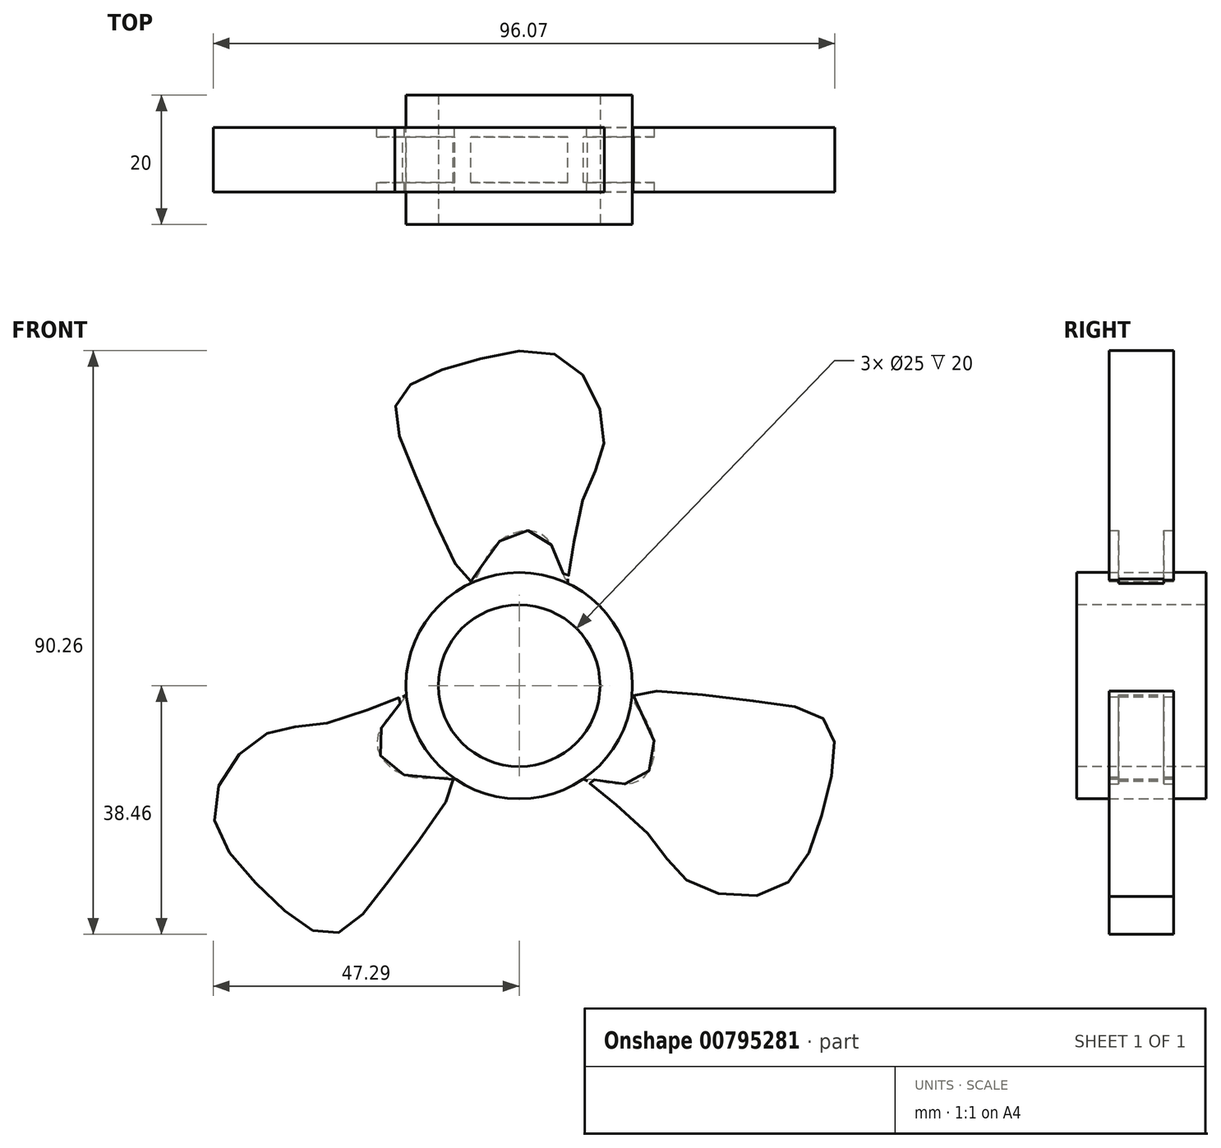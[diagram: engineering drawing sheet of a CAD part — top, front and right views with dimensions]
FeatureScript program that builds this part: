
annotation { "Feature Type Name" : "Feature", "Feature Type Description" : "" }
export const myFeature = defineFeature(function(context is Context, id is Id, definition is map)
    precondition{}
    {
        {
            var Q0;
            Q0=qCreatedBy(makeId("Front.planeOp"),FACE);
            var sketch = newSketch(context, id + "F0", { "sketchPlane" : qUnion([Q0])});
            skCircle(sketch, "E0", {"center": v(0, 0) * mm, "radius": 17.5 * mm});
            skSolve(sketch);
        }
        {
            var Q0;
            Q0=makeQuery(id+"F0.imprint","IMPRINT",FACE,{"disambiguationData":[TD([[makeQuery(id+"F0.imprint","IMPRINT",EDGE,{"derivedFrom":sQuery(id+"F0.wireOp",EDGE,"E0")}),1.0]])]});
            extrude(context, id + "F1", {"entities" : qUnion([Q0]), "endBound" : BoundingType.SYMMETRIC, "depth" : 20 * mm, "offsetDistance" : 25 * mm});
        }
        {
            var Q0;
            Q0=makeQuery(id+"F1.opExtrude","CAP_FACE",FACE,{"disambiguationData":[OSD([sQuery(id+"F0.wireOp",EDGE,"E0")])],"isStart":false});
            var sketch = newSketch(context, id + "F2", { "sketchPlane" : qUnion([Q0])});
            skCircle(sketch, "E1", {"center": v(0, 0) * mm, "radius": 12.5 * mm});
            skSolve(sketch);
        }
        {
            var Q0;
            Q0 = qSketchRegion(id + "F2", true);
            extrude(context, id + "F3", {"entities" : qUnion([Q0]), "operationType" : NewBodyOperationType.REMOVE, "endBound" : BoundingType.THROUGH_ALL, "oppositeDirection" : true, "depth" : 25 * mm, "offsetDistance" : 25 * mm});
        }
        {
            var Q0;
            Q0=qCreatedBy(makeId("Top.planeOp"),FACE);
            cPlane(context, id + "F4", {"entities" : qUnion([Q0]), "cplaneType" : CPlaneType.OFFSET, "offset" : 13 * mm, "width" : 150 * mm, "height" : 150 * mm});
        }
        {
            var Q0;
            Q0=qCreatedBy(id+"F4.planeOp",FACE);
            var sketch = newSketch(context, id + "F5", { "sketchPlane" : qUnion([Q0])});
            skLineSegment(sketch, "E2.bottom", {"start": v(-7.5, 3.5) * mm, "end": v(7.5, 3.5) * mm});
            skLineSegment(sketch, "E2.top", {"start": v(-7.5, -3.5) * mm, "end": v(7.5, -3.5) * mm});
            skLineSegment(sketch, "E2.left", {"start": v(-7.5, 3.5) * mm, "end": v(-7.5, -3.5) * mm});
            skLineSegment(sketch, "E2.right", {"start": v(7.5, 3.5) * mm, "end": v(7.5, -3.5) * mm});
            skPoint(sketch, "E2.middle", {"position": v(0, 0) * mm});
            skSolve(sketch);
        }
        {
            var Q0;
            Q0 = qSketchRegion(id + "F5", true);
            extrude(context, id + "F6", {"entities" : qUnion([Q0]), "operationType" : NewBodyOperationType.ADD, "depth" : 30 * mm, "offsetDistance" : 25 * mm});
        }
        {
            var Q0;
            Q0=qCreatedBy(makeId("Front.planeOp"),FACE);
            var sketch = newSketch(context, id + "F7", { "sketchPlane" : qUnion([Q0])});
            skFitSpline(sketch, "E3", {"points": [v(-7.48, 16.09) * mm, v(-15.55, 31.32) * mm, v(-18.69, 44.54) * mm, v(-7.48, 50.15) * mm, v(7.3, 50.37) * mm, v(13.13, 37.82) * mm, v(9.55, 27.74) * mm, v(7.3, 16.3) * mm, v(3.95, 23.03) * mm, v(-4.12, 21.24) * mm, v(-7.48, 16.09) * mm]});
            skSolve(sketch);
        }
        {
            var Q0;
            Q0=makeQuery(id+"F7.imprint","IMPRINT",FACE,{"disambiguationData":[TD([[makeQuery(id+"F7.imprint","IMPRINT",EDGE,{"derivedFrom":sQuery(id+"F7.wireOp",EDGE,"E3")}),-1.0]])]});
            extrude(context, id + "F8", {"entities" : qUnion([Q0]), "operationType" : NewBodyOperationType.ADD, "endBound" : BoundingType.SYMMETRIC, "depth" : 10 * mm, "offsetDistance" : 25 * mm});
        }
        {
            var Q0;
            Q0=qCreatedBy(makeId("Top.planeOp"),FACE);
            var sketch = newSketch(context, id + "F9", { "sketchPlane" : qUnion([Q0])});
            skLineSegment(sketch, "E4", {"start": v(0, 0) * mm, "end": v(0, 31.06) * mm});
            skLineSegment(sketch, "E5", {"start": v(0, 31.06) * mm, "end": v(0, -34.86) * mm});
            skSolve(sketch);
        }
        {
            var Q0;
            Q0=makeQuery(id+"F1.opExtrude","SWEPT_BODY",BODY,{"disambiguationData":[OSD([sQuery(id+"F0.wireOp",EDGE,"E0")])]});
            var Q1;
            Q1=sQuery(id+"F9.wireOp",EDGE,"E5");
            circularPattern(context, id + "F10", {"entities" : qUnion([Q0]), "axis" : qUnion([Q1]), "angle" : 360 * degree, "instanceCount" : 3, "equalSpace" : true});
        }
    });
